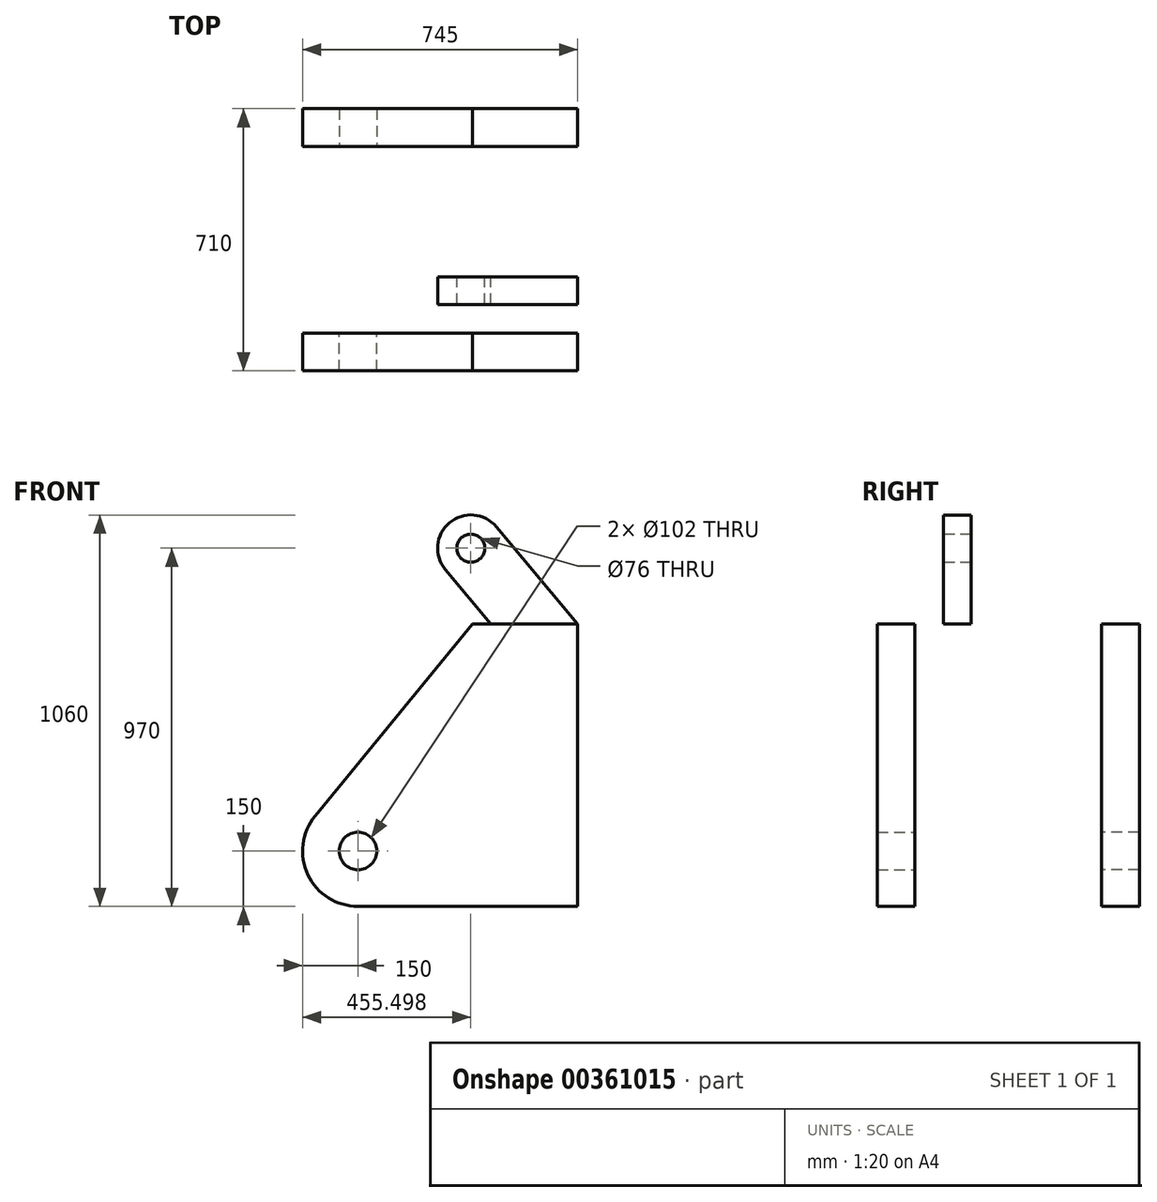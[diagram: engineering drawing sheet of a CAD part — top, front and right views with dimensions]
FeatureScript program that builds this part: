
annotation { "Feature Type Name" : "Feature", "Feature Type Description" : "" }
export const myFeature = defineFeature(function(context is Context, id is Id, definition is map)
    precondition{}
    {
        {
            var Q0;
            Q0=qCreatedBy(makeId("Front.planeOp"),FACE);
            cPlane(context, id + "F0", {"entities" : qUnion([Q0]), "cplaneType" : CPlaneType.OFFSET, "offset" : (506 / 2) * mm, "width" : 150 * mm, "height" : 150 * mm});
        }
        {
            var Q0;
            Q0=qCreatedBy(id+"F0.planeOp",FACE);
            var sketch = newSketch(context, id + "F1", { "sketchPlane" : qUnion([Q0])});
            skLineSegment(sketch, "E0", {"start": v(0, 382.5) * mm, "end": v(0, -382.5) * mm});
            skLineSegment(sketch, "E1", {"start": v(0, 382.5) * mm, "end": v(-285, 382.5) * mm});
            skLineSegment(sketch, "E2", {"start": v(0, -382.5) * mm, "end": v(-595, -382.5) * mm});
            skCircle(sketch, "E3", {"center": v(-595, -232.5) * mm, "radius": 51 * mm});
            skArc(sketch, "E4", {"start": v(-595, -382.5) * mm, "mid": v(-730.57, -296.69) * mm, "end": v(-711.02, -137.43) * mm});
            skLineSegment(sketch, "E5", {"start": v(-285, 382.5) * mm, "end": v(-711.02, -137.43) * mm});
            skSolve(sketch);
        }
        {
            var Q0;
            Q0=makeQuery(id+"F1.imprint","IMPRINT",FACE,{"disambiguationData":[TD([[makeQuery(id+"F1.imprint","IMPRINT",EDGE,{"derivedFrom":sQuery(id+"F1.wireOp",EDGE,"E0")}),-1.0]])]});
            extrude(context, id + "F2", {"entities" : qUnion([Q0]), "depth" : 102 * mm});
        }
        {
            var Q0;
            Q0=makeQuery(id+"F2.opExtrude","SWEPT_BODY",BODY,{"disambiguationData":[OSD([sQuery(id+"F1.wireOp",EDGE,"E0"),sQuery(id+"F1.wireOp",EDGE,"E1"),sQuery(id+"F1.wireOp",EDGE,"E2"),sQuery(id+"F1.wireOp",EDGE,"E3"),sQuery(id+"F1.wireOp",EDGE,"E4"),sQuery(id+"F1.wireOp",EDGE,"E5")])]});
            var Q1;
            Q1=qCreatedBy(makeId("Front.planeOp"),FACE);
            mirror(context, id + "F3", {"entities" : qUnion([Q0]), "mirrorPlane" : qUnion([Q1])});
        }
        {
            var Q0;
            Q0=makeQuery(id+"F2.opExtrude","SWEPT_FACE",FACE,{"disambiguationData":[OSD([sQuery(id+"F1.wireOp",EDGE,"E1")])]});
            var sketch = newSketch(context, id + "F4", { "sketchPlane" : qUnion([Q0])});
            skLineSegment(sketch, "E6.0", {"start": v(0, 355) * mm, "end": v(-285, 355) * mm});
            skLineSegment(sketch, "E7.bottom", {"start": v(-285, -355) * mm, "end": v(0, -355) * mm});
            skLineSegment(sketch, "E7.top", {"start": v(-285, 355) * mm, "end": v(0, 355) * mm});
            skLineSegment(sketch, "E7.left", {"start": v(-285, -355) * mm, "end": v(-285, 355) * mm});
            skCircle(sketch, "E8", {"center": v(210, 0) * mm, "radius": 75 * mm});
            skArc(sketch, "E9", {"start": v(311.23, 178.26) * mm, "mid": v(415, 0) * mm, "end": v(311.23, -178.26) * mm});
            skLineSegment(sketch, "E10", {"start": v(0, 355) * mm, "end": v(311.23, 178.26) * mm});
            skLineSegment(sketch, "E11", {"start": v(0, -355) * mm, "end": v(311.23, -178.26) * mm});
            skSolve(sketch);
        }
        {
            var Q0;
            {var subQ0=sQuery(id+"F4.wireOp",EDGE,"E7.bottom");Q0=makeQuery(id+"F4.imprint","IMPRINT",FACE,{"disambiguationData":[TD([[makeQuery(id+"F4.imprint","IMPRINT",EDGE,{"derivedFrom":subQ0}),-1.0]])]});}
            var Q1;
            {var subQ3=sQuery(id+"F4.wireOp",EDGE,"E7.top");Q1=makeQuery(id+"F4.imprint","IMPRINT",FACE,{"disambiguationData":[TD([[makeQuery(id+"F4.imprint","IMPRINT",EDGE,{"derivedFrom":subQ3}),-1.0]])]});}
            extrude(context, id + "F5", {"entities" : qUnion([Q0, Q1]), "oppositeDirection" : true, "depth" : 102 * mm});
        }
        {
            var Q0;
            Q0=makeQuery(id+"F5.opExtrude","SWEPT_BODY",BODY,{"disambiguationData":[OSD([sQuery(id+"F4.wireOp",EDGE,"E7.bottom"),sQuery(id+"F4.wireOp",EDGE,"E7.top"),sQuery(id+"F4.wireOp",EDGE,"E7.left"),sQuery(id+"F4.wireOp",EDGE,"E8"),sQuery(id+"F4.wireOp",EDGE,"E9"),sQuery(id+"F4.wireOp",EDGE,"E10"),sQuery(id+"F4.wireOp",EDGE,"E11")])]});
            var Q1;
            Q1=qCreatedBy(makeId("Top.planeOp"),FACE);
            mirror(context, id + "F6", {"entities" : qUnion([Q0]), "mirrorPlane" : qUnion([Q1])});
        }
        {
            var Q0;
            Q0=makeQuery(id+"F6.opPattern","COPY",BODY,{"derivedFrom":makeQuery(id+"F5.opExtrude","SWEPT_BODY",BODY,{"disambiguationData":[OSD([sQuery(id+"F4.wireOp",EDGE,"E7.bottom"),sQuery(id+"F4.wireOp",EDGE,"E7.top"),sQuery(id+"F4.wireOp",EDGE,"E7.left"),sQuery(id+"F4.wireOp",EDGE,"E8"),sQuery(id+"F4.wireOp",EDGE,"E9"),sQuery(id+"F4.wireOp",EDGE,"E10"),sQuery(id+"F4.wireOp",EDGE,"E11")])]}),"instanceName":"1"});
            var Q1;
            Q1=makeQuery(id+"F2.opExtrude","SWEPT_BODY",BODY,{"disambiguationData":[OSD([sQuery(id+"F1.wireOp",EDGE,"E0"),sQuery(id+"F1.wireOp",EDGE,"E1"),sQuery(id+"F1.wireOp",EDGE,"E2"),sQuery(id+"F1.wireOp",EDGE,"E3"),sQuery(id+"F1.wireOp",EDGE,"E4"),sQuery(id+"F1.wireOp",EDGE,"E5")])]});
            var Q2;
            Q2=makeQuery(id+"F3.opPattern","COPY",BODY,{"derivedFrom":makeQuery(id+"F2.opExtrude","SWEPT_BODY",BODY,{"disambiguationData":[OSD([sQuery(id+"F1.wireOp",EDGE,"E0"),sQuery(id+"F1.wireOp",EDGE,"E1"),sQuery(id+"F1.wireOp",EDGE,"E2"),sQuery(id+"F1.wireOp",EDGE,"E3"),sQuery(id+"F1.wireOp",EDGE,"E4"),sQuery(id+"F1.wireOp",EDGE,"E5")])]}),"instanceName":"1"});
            var Q3;
            Q3=makeQuery(id+"F5.opExtrude","SWEPT_BODY",BODY,{"disambiguationData":[OSD([sQuery(id+"F4.wireOp",EDGE,"E7.bottom"),sQuery(id+"F4.wireOp",EDGE,"E7.top"),sQuery(id+"F4.wireOp",EDGE,"E7.left"),sQuery(id+"F4.wireOp",EDGE,"E8"),sQuery(id+"F4.wireOp",EDGE,"E9"),sQuery(id+"F4.wireOp",EDGE,"E10"),sQuery(id+"F4.wireOp",EDGE,"E11")])]});
            booleanBodies(context, id + "F7", {"operationType" : BooleanOperationType.UNION, "tools" : qUnion([Q0, Q1, Q2, Q3])});
        }
        {
            var Q0;
            Q0=qCreatedBy(makeId("Front.planeOp"),FACE);
            cPlane(context, id + "F8", {"entities" : qUnion([Q0]), "cplaneType" : CPlaneType.OFFSET, "offset" : 100 * mm, "width" : 150 * mm, "height" : 150 * mm});
        }
        {
            var Q0;
            Q0=qCreatedBy(id+"F8.planeOp",FACE);
            var sketch = newSketch(context, id + "F9", { "sketchPlane" : qUnion([Q0])});
            skLineSegment(sketch, "E12.0", {"start": v(311.23, 382.5) * mm, "end": v(415, 382.5) * mm});
            skLineSegment(sketch, "E13.0", {"start": v(0, 382.5) * mm, "end": v(311.23, 382.5) * mm});
            skLineSegment(sketch, "E14", {"start": v(0, 382.5) * mm, "end": v(-220.56, 645.35) * mm});
            skArc(sketch, "E15", {"start": v(-220.56, 645.35) * mm, "mid": v(-347.35, 656.44) * mm, "end": v(-358.45, 529.65) * mm});
            skLineSegment(sketch, "E16", {"start": v(-358.45, 529.65) * mm, "end": v(-234.97, 382.5) * mm});
            skCircle(sketch, "E17", {"center": v(-289.5, 587.5) * mm, "radius": 38 * mm});
            skLineSegment(sketch, "E18", {"start": v(-234.97, 382.5) * mm, "end": v(0, 382.5) * mm});
            skSolve(sketch);
        }
        {
            var Q0;
            Q0=makeQuery(id+"F9.imprint","IMPRINT",FACE,{"disambiguationData":[TD([[makeQuery(id+"F9.imprint","IMPRINT",EDGE,{"derivedFrom":sQuery(id+"F9.wireOp",EDGE,"E14")}),1.0]])]});
            extrude(context, id + "F10", {"entities" : qUnion([Q0]), "operationType" : NewBodyOperationType.ADD, "depth" : 75 * mm});
        }
    });
